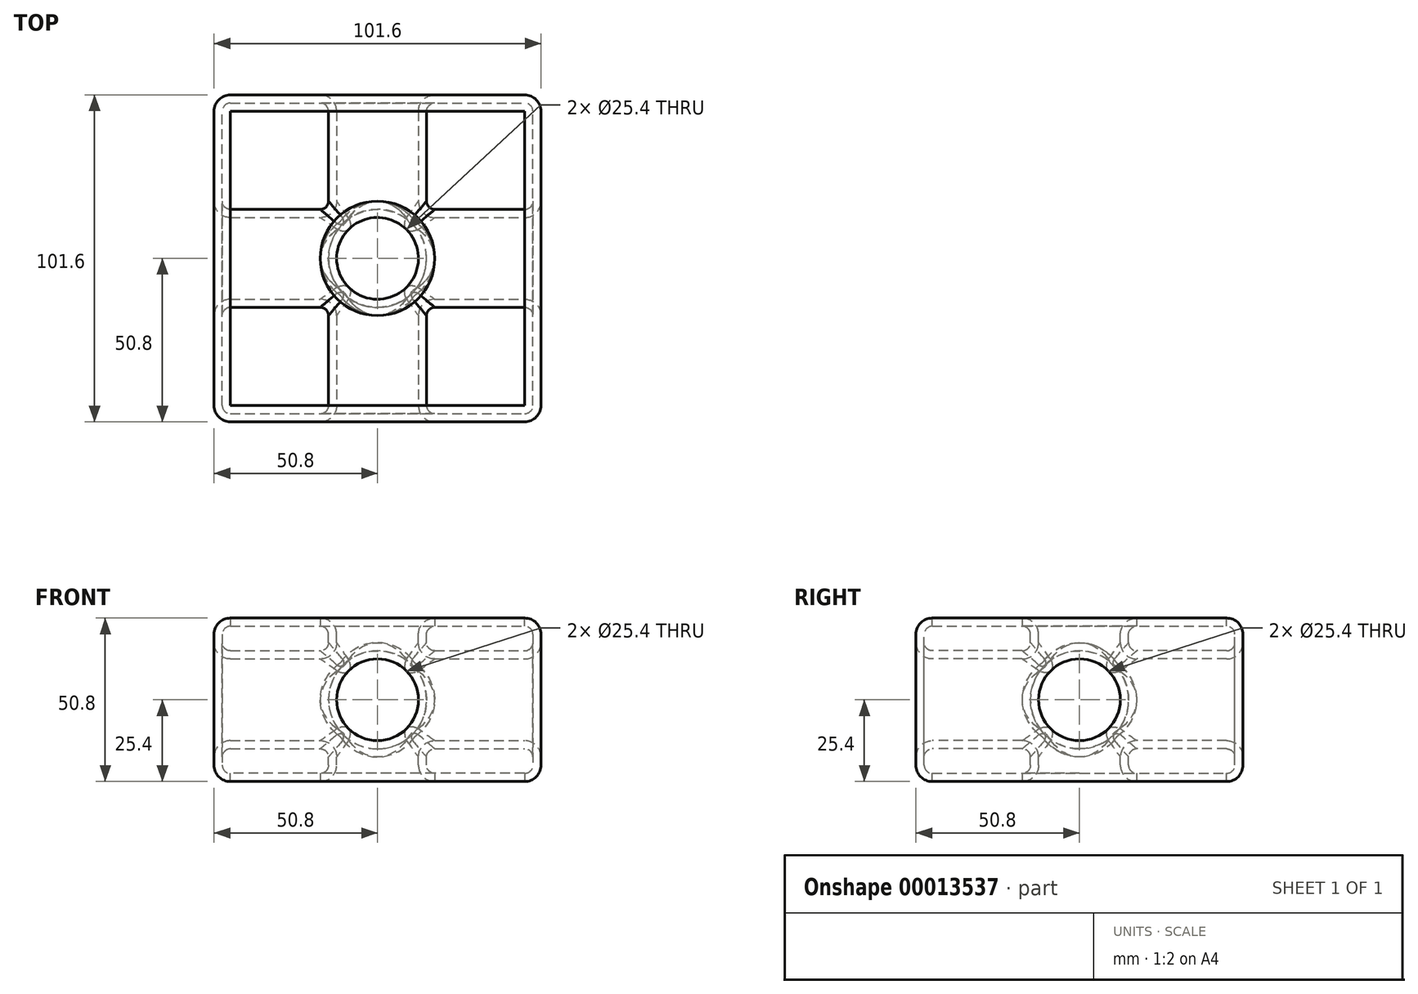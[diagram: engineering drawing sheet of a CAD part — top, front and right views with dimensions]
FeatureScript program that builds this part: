
annotation { "Feature Type Name" : "Feature", "Feature Type Description" : "" }
export const myFeature = defineFeature(function(context is Context, id is Id, definition is map)
    precondition{}
    {
        {
            var Q0;
            Q0=qCreatedBy(makeId("Front.planeOp"),FACE);
            var sketch = newSketch(context, id + "F0", { "sketchPlane" : qUnion([Q0])});
            skLineSegment(sketch, "E0.rect.bottom", {"start": v(50.8, 25.4) * mm, "end": v(-50.8, 25.4) * mm});
            skLineSegment(sketch, "E0.rect.top", {"start": v(50.8, -25.4) * mm, "end": v(-50.8, -25.4) * mm});
            skLineSegment(sketch, "E0.rect.left", {"start": v(50.8, 25.4) * mm, "end": v(50.8, -25.4) * mm});
            skLineSegment(sketch, "E0.rect.right", {"start": v(-50.8, 25.4) * mm, "end": v(-50.8, -25.4) * mm});
            skPoint(sketch, "E0.rect.middle", {"position": v(0, 0) * mm});
            skSolve(sketch);
        }
        {
            var Q0;
            Q0 = qSketchRegion(id + "F0", true);
            extrude(context, id + "F1", {"entities" : qUnion([Q0]), "depth" : 101.6 * mm});
        }
        {
            var Q0;
            Q0=makeQuery(id+"F1.opExtrude","SWEPT_FACE",FACE,{"disambiguationData":[OSD([sQuery(id+"F0.wireOp",EDGE,"E0.rect.left")])]});
            var sketch = newSketch(context, id + "F2", { "sketchPlane" : qUnion([Q0])});
            skCircle(sketch, "E1", {"center": v(-50.8, 0) * mm, "radius": 12.7 * mm});
            skSolve(sketch);
        }
        {
            var Q0;
            Q0 = qSketchRegion(id + "F2", true);
            extrude(context, id + "F3", {"entities" : qUnion([Q0]), "operationType" : NewBodyOperationType.REMOVE, "endBound" : BoundingType.THROUGH_ALL, "oppositeDirection" : true, "depth" : 25.4 * mm});
        }
        {
            var Q0;
            Q0=makeQuery(id+"F1.opExtrude","SWEPT_FACE",FACE,{"disambiguationData":[OSD([sQuery(id+"F0.wireOp",EDGE,"E0.rect.bottom")])]});
            var sketch = newSketch(context, id + "F4", { "sketchPlane" : qUnion([Q0])});
            skCircle(sketch, "E2", {"center": v(0, -50.8) * mm, "radius": 12.7 * mm});
            skSolve(sketch);
        }
        {
            var Q0;
            Q0 = qSketchRegion(id + "F4", true);
            extrude(context, id + "F5", {"entities" : qUnion([Q0]), "operationType" : NewBodyOperationType.REMOVE, "endBound" : BoundingType.THROUGH_ALL, "oppositeDirection" : true, "depth" : 25.4 * mm});
        }
        {
            var Q0;
            Q0=makeQuery(id+"F1.opExtrude","CAP_FACE",FACE,{"disambiguationData":[OSD([sQuery(id+"F0.wireOp",EDGE,"E0.rect.bottom"),sQuery(id+"F0.wireOp",EDGE,"E0.rect.top"),sQuery(id+"F0.wireOp",EDGE,"E0.rect.left"),sQuery(id+"F0.wireOp",EDGE,"E0.rect.right")])],"isStart":false});
            var sketch = newSketch(context, id + "F6", { "sketchPlane" : qUnion([Q0])});
            skCircle(sketch, "E3", {"center": v(0, 0) * mm, "radius": 12.7 * mm});
            skSolve(sketch);
        }
        {
            var Q0;
            Q0 = qSketchRegion(id + "F6", true);
            extrude(context, id + "F7", {"entities" : qUnion([Q0]), "operationType" : NewBodyOperationType.REMOVE, "endBound" : BoundingType.THROUGH_ALL, "oppositeDirection" : true, "depth" : 25.4 * mm});
        }
        {
            var Q0;
            Q0=makeQuery(id+"F1.opExtrude","CAP_FACE",FACE,{"disambiguationData":[OSD([sQuery(id+"F0.wireOp",EDGE,"E0.rect.bottom"),sQuery(id+"F0.wireOp",EDGE,"E0.rect.top"),sQuery(id+"F0.wireOp",EDGE,"E0.rect.left"),sQuery(id+"F0.wireOp",EDGE,"E0.rect.right")])],"isStart":false});
            var Q1;
            Q1=makeQuery(id+"F1.opExtrude","SWEPT_FACE",FACE,{"disambiguationData":[OSD([sQuery(id+"F0.wireOp",EDGE,"E0.rect.left")])]});
            var Q2;
            Q2=makeQuery(id+"F1.opExtrude","SWEPT_FACE",FACE,{"disambiguationData":[OSD([sQuery(id+"F0.wireOp",EDGE,"E0.rect.bottom")])]});
            var Q3;
            Q3=makeQuery(id+"F1.opExtrude","SWEPT_FACE",FACE,{"disambiguationData":[OSD([sQuery(id+"F0.wireOp",EDGE,"E0.rect.right")])]});
            var Q4;
            Q4=makeQuery(id+"F1.opExtrude","SWEPT_FACE",FACE,{"disambiguationData":[OSD([sQuery(id+"F0.wireOp",EDGE,"E0.rect.top")])]});
            fillet(context, id + "F8", {"entities" : qUnion([Q0, Q1, Q2, Q3, Q4]), "radius" : 5.08 * mm, "tangentPropagation" : true, "allowEdgeOverflow" : false});
        }
        {
            var Q0;
            Q0=makeQuery(id+"F7.boolean.opBoolean","INTERSECT",EDGE,{"derivedFrom":[makeQuery(id+"F1.opExtrude","CAP_FACE",FACE,{"disambiguationData":[OSD([sQuery(id+"F0.wireOp",EDGE,"E0.rect.bottom"),sQuery(id+"F0.wireOp",EDGE,"E0.rect.top"),sQuery(id+"F0.wireOp",EDGE,"E0.rect.left"),sQuery(id+"F0.wireOp",EDGE,"E0.rect.right")])],"isStart":true}),makeQuery(id+"F7.opExtrude","SWEPT_FACE",FACE,{"disambiguationData":[OSD([sQuery(id+"F6.wireOp",EDGE,"E3")])]})]});
            var Q1;
            Q1=makeQuery(id+"F5.boolean.opBoolean","COPY",FACE,{"disambiguationData":[OD(1.0)],"derivedFrom":makeQuery(id+"F5.opExtrude","SWEPT_FACE",FACE,{"disambiguationData":[OSD([sQuery(id+"F4.wireOp",EDGE,"E2")])]})});
            var Q2;
            Q2=makeQuery(id+"F7.boolean.opBoolean","COPY",FACE,{"disambiguationData":[OD(1.0)],"derivedFrom":makeQuery(id+"F7.opExtrude","SWEPT_FACE",FACE,{"disambiguationData":[OSD([sQuery(id+"F6.wireOp",EDGE,"E3")])]})});
            var Q3;
            Q3=makeQuery(id+"F5.boolean.opBoolean","COPY",FACE,{"disambiguationData":[OD(0.0)],"derivedFrom":makeQuery(id+"F5.opExtrude","SWEPT_FACE",FACE,{"disambiguationData":[OSD([sQuery(id+"F4.wireOp",EDGE,"E2")])]})});
            var Q4;
            {var subQ0=makeQuery(id+"F3.boolean.opBoolean","COPY",FACE,{"derivedFrom":makeQuery(id+"F3.opExtrude","SWEPT_FACE",FACE,{"disambiguationData":[OSD([sQuery(id+"F2.wireOp",EDGE,"E1")])]})});Q4=makeQuery(id+"F5.boolean.opBoolean","SPLIT",FACE,{"disambiguationData":[TD([makeQuery(id+"F1.opExtrude","SWEPT_FACE",FACE,{"disambiguationData":[OSD([sQuery(id+"F0.wireOp",EDGE,"E0.rect.right")])]})])],"derivedFrom":subQ0});}
            var Q5;
            Q5=makeQuery(id+"F7.boolean.opBoolean","COPY",FACE,{"disambiguationData":[OD(0.0)],"derivedFrom":makeQuery(id+"F7.opExtrude","SWEPT_FACE",FACE,{"disambiguationData":[OSD([sQuery(id+"F6.wireOp",EDGE,"E3")])]})});
            fillet(context, id + "F9", {"entities" : qUnion([Q0, Q1, Q2, Q3, Q4, Q5]), "radius" : 5.08 * mm, "tangentPropagation" : true, "allowEdgeOverflow" : false});
        }
        {
            var Q0;
            Q0=makeQuery(id+"F1.opExtrude","SWEPT_FACE",FACE,{"disambiguationData":[OSD([sQuery(id+"F0.wireOp",EDGE,"E0.rect.bottom")])]});
            var Q1;
            Q1=makeQuery(id+"F1.opExtrude","SWEPT_FACE",FACE,{"disambiguationData":[OSD([sQuery(id+"F0.wireOp",EDGE,"E0.rect.top")])]});
            var Q2;
            Q2=makeQuery(id+"F1.opExtrude","SWEPT_BODY",BODY,{"disambiguationData":[OSD([sQuery(id+"F0.wireOp",EDGE,"E0.rect.bottom"),sQuery(id+"F0.wireOp",EDGE,"E0.rect.top"),sQuery(id+"F0.wireOp",EDGE,"E0.rect.left"),sQuery(id+"F0.wireOp",EDGE,"E0.rect.right")])]});
            shell(context, id + "F10", {"entities" : qUnion([Q0, Q1]), "parts" : qUnion([Q2]), "thickness" : 2.54 * mm});
        }
    });
